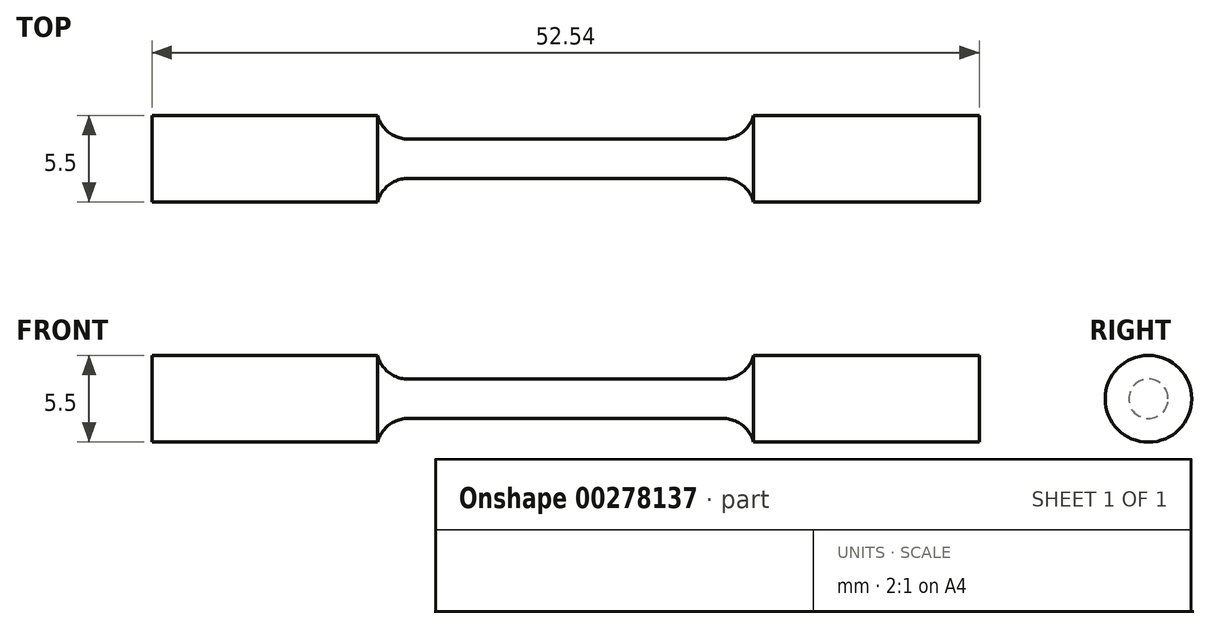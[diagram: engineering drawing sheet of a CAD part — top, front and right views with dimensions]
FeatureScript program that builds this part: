
annotation { "Feature Type Name" : "Feature", "Feature Type Description" : "" }
export const myFeature = defineFeature(function(context is Context, id is Id, definition is map)
    precondition{}
    {
        {
            var Q0;
            Q0=qCreatedBy(makeId("Front.planeOp"),FACE);
            var sketch = newSketch(context, id + "F0", { "sketchPlane" : qUnion([Q0])});
            skLineSegment(sketch, "E0", {"start": v(0, 1.25) * mm, "end": v(10, 1.25) * mm});
            skArc(sketch, "E1", {"start": v(10, 1.25) * mm, "mid": v(11.23, 1.67) * mm, "end": v(11.94, 2.75) * mm});
            skLineSegment(sketch, "E2", {"start": v(11.94, 2.75) * mm, "end": v(26.27, 2.75) * mm});
            skLineSegment(sketch, "E3", {"start": v(26.27, 2.75) * mm, "end": v(26.27, 0) * mm});
            skLineSegment(sketch, "E4.MirrorCS", {"start": v(0, 1.25) * mm, "end": v(-10, 1.25) * mm});
            skLineSegment(sketch, "E5.MirrorCS", {"start": v(-26.27, 2.75) * mm, "end": v(-26.27, 0) * mm});
            skLineSegment(sketch, "E6.MirrorCS", {"start": v(-11.94, 2.75) * mm, "end": v(-26.27, 2.75) * mm});
            skArc(sketch, "E7.MirrorCS", {"start": v(-10, 1.25) * mm, "mid": v(-11.23, 1.67) * mm, "end": v(-11.94, 2.75) * mm});
            skLineSegment(sketch, "E8", {"start": v(-26.27, 0) * mm, "end": v(26.27, 0) * mm});
            skSolve(sketch);
        }
        {
            var Q0;
            Q0 = qSketchRegion(id + "F0", true);
            var Q1;
            Q1=sQuery(id+"F0.wireOp",EDGE,"E8");
            revolve(context, id + "F1", {"entities" : qUnion([Q0]), "axis" : qUnion([Q1]), "revolveType" : RevolveType.FULL});
        }
    });
